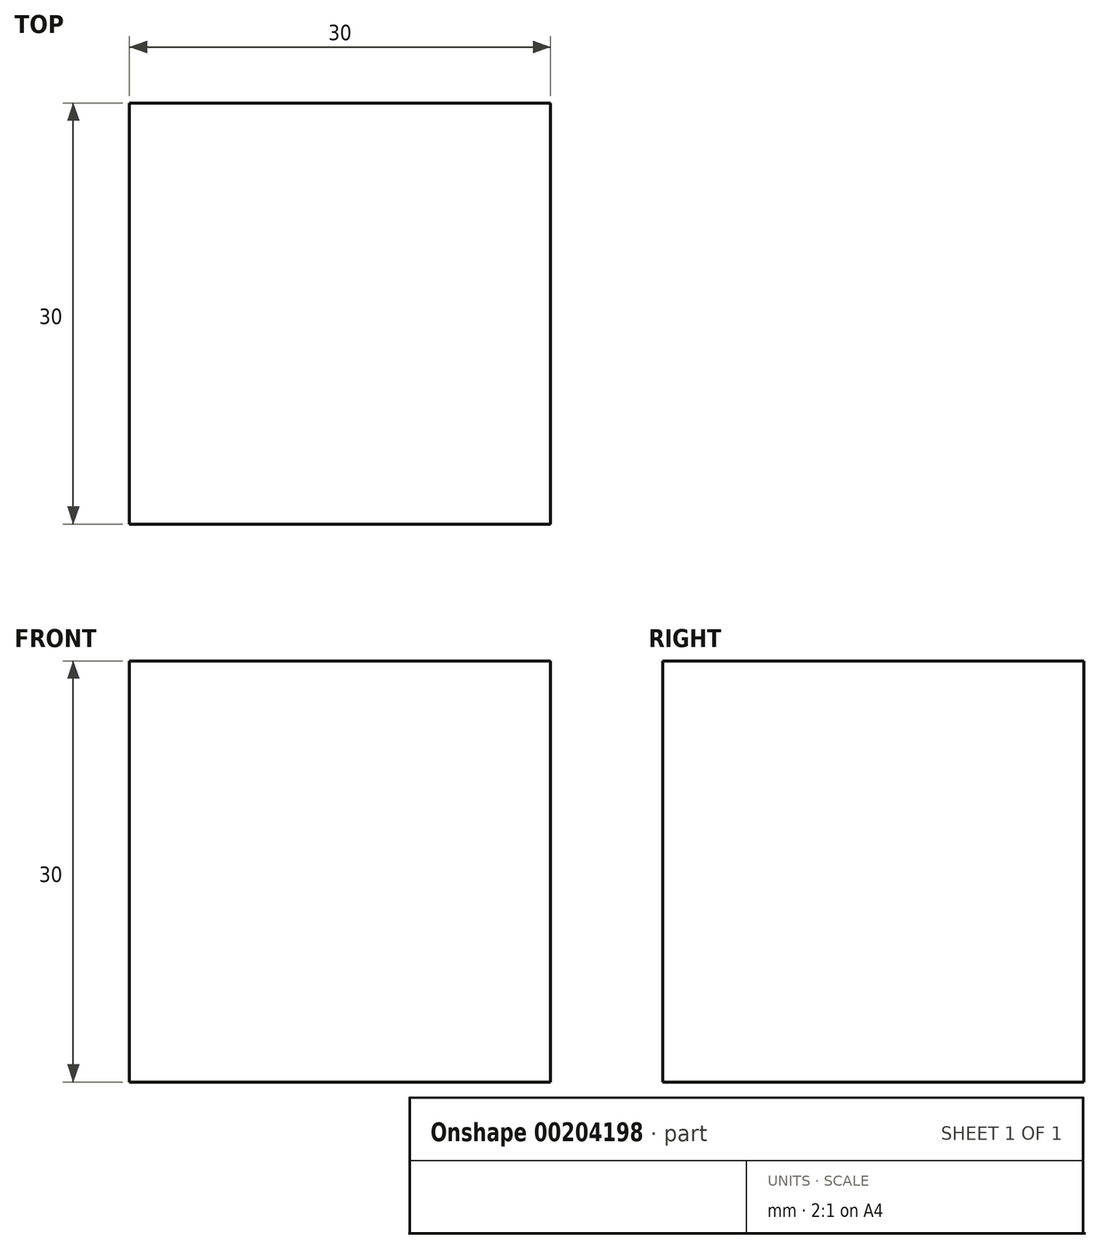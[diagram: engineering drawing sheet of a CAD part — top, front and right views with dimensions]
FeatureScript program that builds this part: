
annotation { "Feature Type Name" : "Feature", "Feature Type Description" : "" }
export const myFeature = defineFeature(function(context is Context, id is Id, definition is map)
    precondition{}
    {
        {
            var Q0;
            Q0=qCreatedBy(makeId("Top.planeOp"),FACE);
            var sketch = newSketch(context, id + "F0", { "sketchPlane" : qUnion([Q0])});
            skLineSegment(sketch, "E0.bottom", {"start": v(15, 15) * mm, "end": v(-15, 15) * mm});
            skLineSegment(sketch, "E0.top", {"start": v(-15, -15) * mm, "end": v(15, -15) * mm});
            skLineSegment(sketch, "E0.left", {"start": v(-15, 15) * mm, "end": v(-15, -15) * mm});
            skLineSegment(sketch, "E0.right", {"start": v(15, 15) * mm, "end": v(15, -15) * mm});
            skPoint(sketch, "E0.middle", {"position": v(0, 0) * mm});
            skSolve(sketch);
        }
        {
            var Q0;
            Q0=makeQuery(id+"F0.imprint","IMPRINT",FACE,{"disambiguationData":[TD([[makeQuery(id+"F0.imprint","IMPRINT",EDGE,{"derivedFrom":sQuery(id+"F0.wireOp",EDGE,"E0.bottom")}),1.0]])]});
            extrude(context, id + "F1", {"entities" : qUnion([Q0]), "depth" : 30 * mm});
        }
    });
